# Revit family: Lighting-Proiezione-GEWISS-ESALITE-PL-PROIETTORI-LED_16K_DALI
name_source: partatom
category: Apparecchi per illuminazione
units: mm (PartAtom-declared; Revit-internal decimal feet)

## family parameters
Condiviso = No
Host = Superficie
Punto di calcolo locali = Sì
Quota connettore circolare = Usa diametro
Sorgente d'illuminazione = No
Taglio con vuoti quando caricato = No
Tipo di parte = Normale

## types (1)
- Lighting-Proiezione-GEWISS-ESALITE-PL-PROIETTORI-LED_16K_DALI
    Applicazione = Interno / Esterno
    Base = corpo luce
    Catalogo = LIGHTING
    Catalogo Serie = ESALITE PL - 16K
    Classe di efficienza LED integrati = A ÷ A++
    Classe isolamento = I
    Codice Electrocod = 2444
    Colore = Grigio RAL 9006
    Corrente di pilotaggio. = 0,599999999999999A
    Descrizione = ESALITE 16K ELL.5700K GIU+V.GR.DALI
    Flusso nominale (lm) = 17000
    Garanzia = 5 anni
    Grado di protezione = IP66
    IDF = c6fec43f-92ff-4fa4-a2dc-3846b0604e57
    IDT = 7261efcd332c45799459aa82df75d831
    Immagine tipo = ESALITE_PL.jpg
    Lampada: = LED - Non sostituibile
    Life time L90B10 (Tq 25°C) = 100000H
    Life time L90B10 (Tq 50°C) = 50000H
    Lumen output (lm) = 13600
    Modello = GWS6535GD57K
    Numero poli = 1
    Ottica = Ellittica
    Peso (kg): = 8,5
    Potenza di sistema = 125W
    Potenza di sitema = Wxxx
    Produttore = GEWISS S.p.A.
    Prospetto di default = 1219 mm
    Resistenza agli urti = IK08
    Resistenza alle sovratensioni : = 8KV in modalità comune; 6KV in modalità differenziale
    SEO = Proiettore
    Scheda Tecnica = https://www.gewiss.com
    Schermo = Vetro temprato
    Spostamento_x_simb = 0 mm  [stored 0 ft]
    Spostamento_x_simb_effettivo = 4000 mm  [stored 13.1234 ft]
    Temperatura di colore: = 5700 K (CRI>80)
    Temperatura di utilizzo = -30 +50 °C
    Tensione = 220/240 V - 50/60 Hz
    Tipo alimentatore = Driver Led Dali
    URL = https://www.gewiss.com
    V = 0 V
    Versione file RFA = 20.11
    Versioni = Luce fredda 5700K

note: [stored X ft] marks values corroborated as IEEE doubles in the binary element streams (Revit-internal decimal feet)
